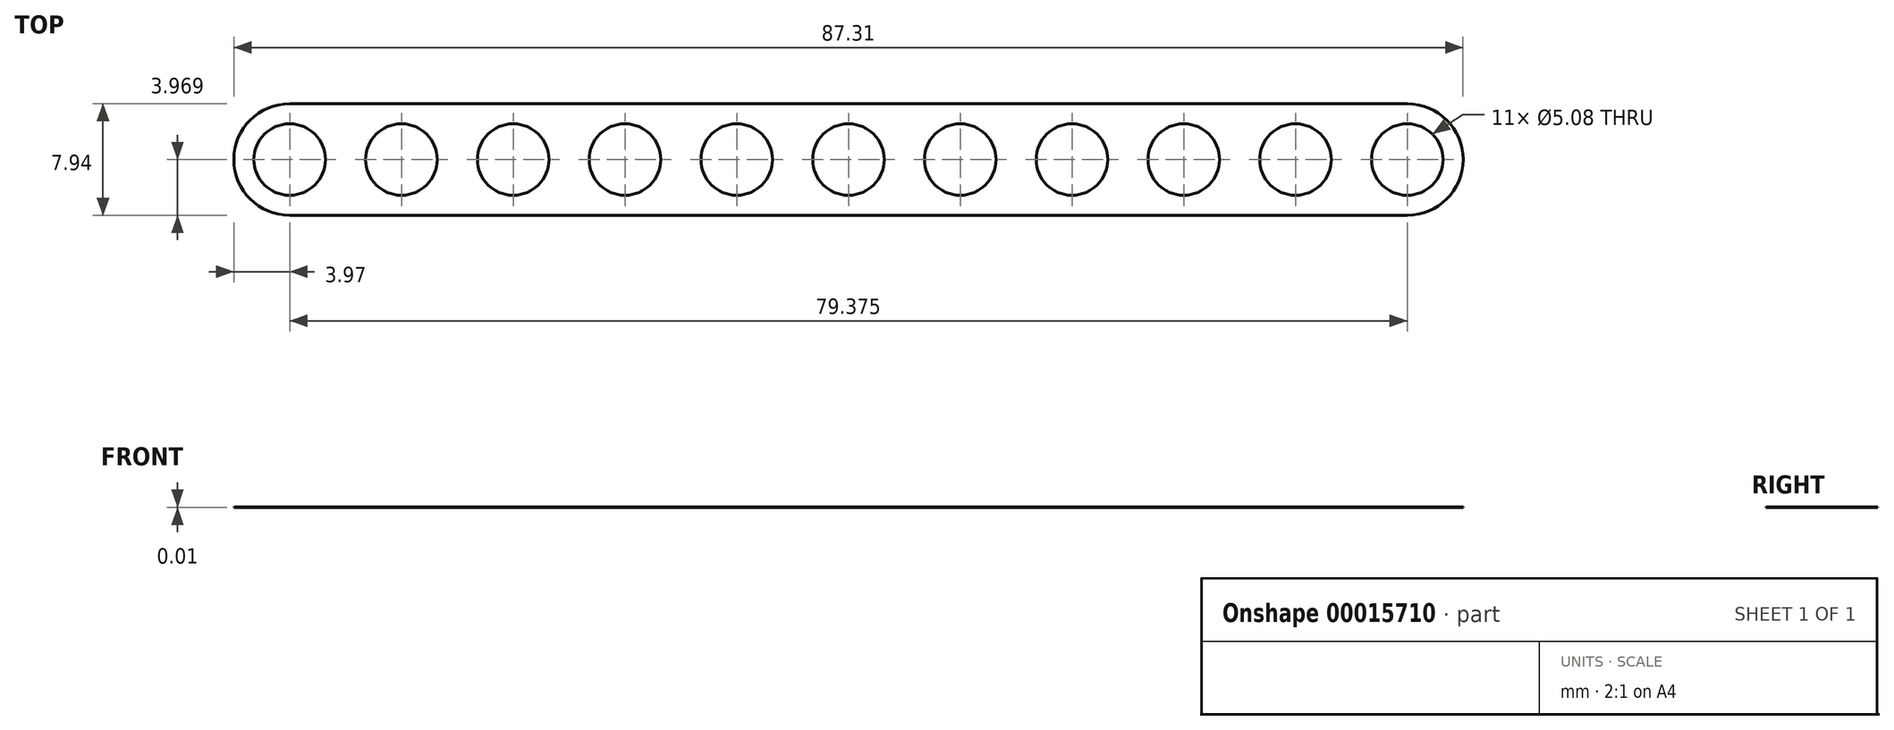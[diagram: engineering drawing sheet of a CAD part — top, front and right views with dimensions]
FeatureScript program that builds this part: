
annotation { "Feature Type Name" : "Feature", "Feature Type Description" : "" }
export const myFeature = defineFeature(function(context is Context, id is Id, definition is map)
    precondition{}
    {
        {
            var Q0;
            Q0=qCreatedBy(makeId("Top.planeOp"),FACE);
            var sketch = newSketch(context, id + "F0", { "sketchPlane" : qUnion([Q0])});
            skLineSegment(sketch, "E0.bottom", {"start": v(0, 0) * mm, "end": v(79.38, 0) * mm});
            skLineSegment(sketch, "E0.top", {"start": v(0, 7.94) * mm, "end": v(79.37, 7.94) * mm});
            skLineSegment(sketch, "E0.left", {"start": v(0, 0) * mm, "end": v(0, 7.94) * mm});
            skLineSegment(sketch, "E0.right", {"start": v(79.38, 0) * mm, "end": v(79.38, 7.94) * mm});
            skCircle(sketch, "E1", {"center": v(79.38, 3.97) * mm, "radius": 2.54 * mm});
            skCircle(sketch, "E2", {"center": v(7.94, 3.97) * mm, "radius": 2.54 * mm});
            skCircle(sketch, "E3", {"center": v(0, 3.97) * mm, "radius": 2.54 * mm});
            skLineSegment(sketch, "E4", {"start": v(7.94, 3.97) * mm, "end": v(0, 3.97) * mm});
            skArc(sketch, "E5", {"start": v(79.38, 0) * mm, "mid": v(83.34, 3.97) * mm, "end": v(79.37, 7.94) * mm});
            skArc(sketch, "E6", {"start": v(0, 7.94) * mm, "mid": v(-3.97, 3.97) * mm, "end": v(0, 0) * mm});
            skLineSegment(sketch, "E7", {"start": v(7.94, 3.97) * mm, "end": v(15.88, 3.97) * mm});
            skLineSegment(sketch, "E8", {"start": v(15.88, 3.97) * mm, "end": v(23.81, 3.97) * mm});
            skLineSegment(sketch, "E9", {"start": v(47.62, 3.97) * mm, "end": v(55.56, 3.97) * mm});
            skLineSegment(sketch, "E10", {"start": v(55.56, 3.97) * mm, "end": v(63.5, 3.97) * mm});
            skLineSegment(sketch, "E11", {"start": v(63.5, 3.97) * mm, "end": v(71.44, 3.97) * mm});
            skLineSegment(sketch, "E12", {"start": v(71.44, 3.97) * mm, "end": v(79.38, 3.97) * mm});
            skCircle(sketch, "E13", {"center": v(15.88, 3.97) * mm, "radius": 2.54 * mm});
            skCircle(sketch, "E14", {"center": v(23.81, 3.97) * mm, "radius": 2.54 * mm});
            skCircle(sketch, "E15", {"center": v(47.62, 3.97) * mm, "radius": 2.54 * mm});
            skCircle(sketch, "E16", {"center": v(55.56, 3.97) * mm, "radius": 2.54 * mm});
            skCircle(sketch, "E17", {"center": v(63.5, 3.97) * mm, "radius": 2.54 * mm});
            skCircle(sketch, "E18", {"center": v(71.44, 3.97) * mm, "radius": 2.54 * mm});
            skLineSegment(sketch, "E19", {"start": v(47.62, 3.97) * mm, "end": v(39.69, 3.97) * mm, "construction": true});
            skLineSegment(sketch, "E20", {"start": v(39.69, 3.97) * mm, "end": v(31.75, 3.97) * mm, "construction": true});
            skLineSegment(sketch, "E21", {"start": v(31.75, 3.97) * mm, "end": v(23.81, 3.97) * mm});
            skCircle(sketch, "E22", {"center": v(31.75, 3.97) * mm, "radius": 2.54 * mm});
            skCircle(sketch, "E23", {"center": v(39.69, 3.97) * mm, "radius": 2.54 * mm});
            skLineSegment(sketch, "E24", {"start": v(39.69, 7.94) * mm, "end": v(39.69, 0) * mm, "construction": true});
            skSolve(sketch);
        }
        {
            var Q0;
            Q0=qSketchRegion(id+"F0",true);
            extrude(context, id + "F1", {"entities" : qUnion([Q0]), "depth" : 5 / 406.4 * mm});
        }
    });
